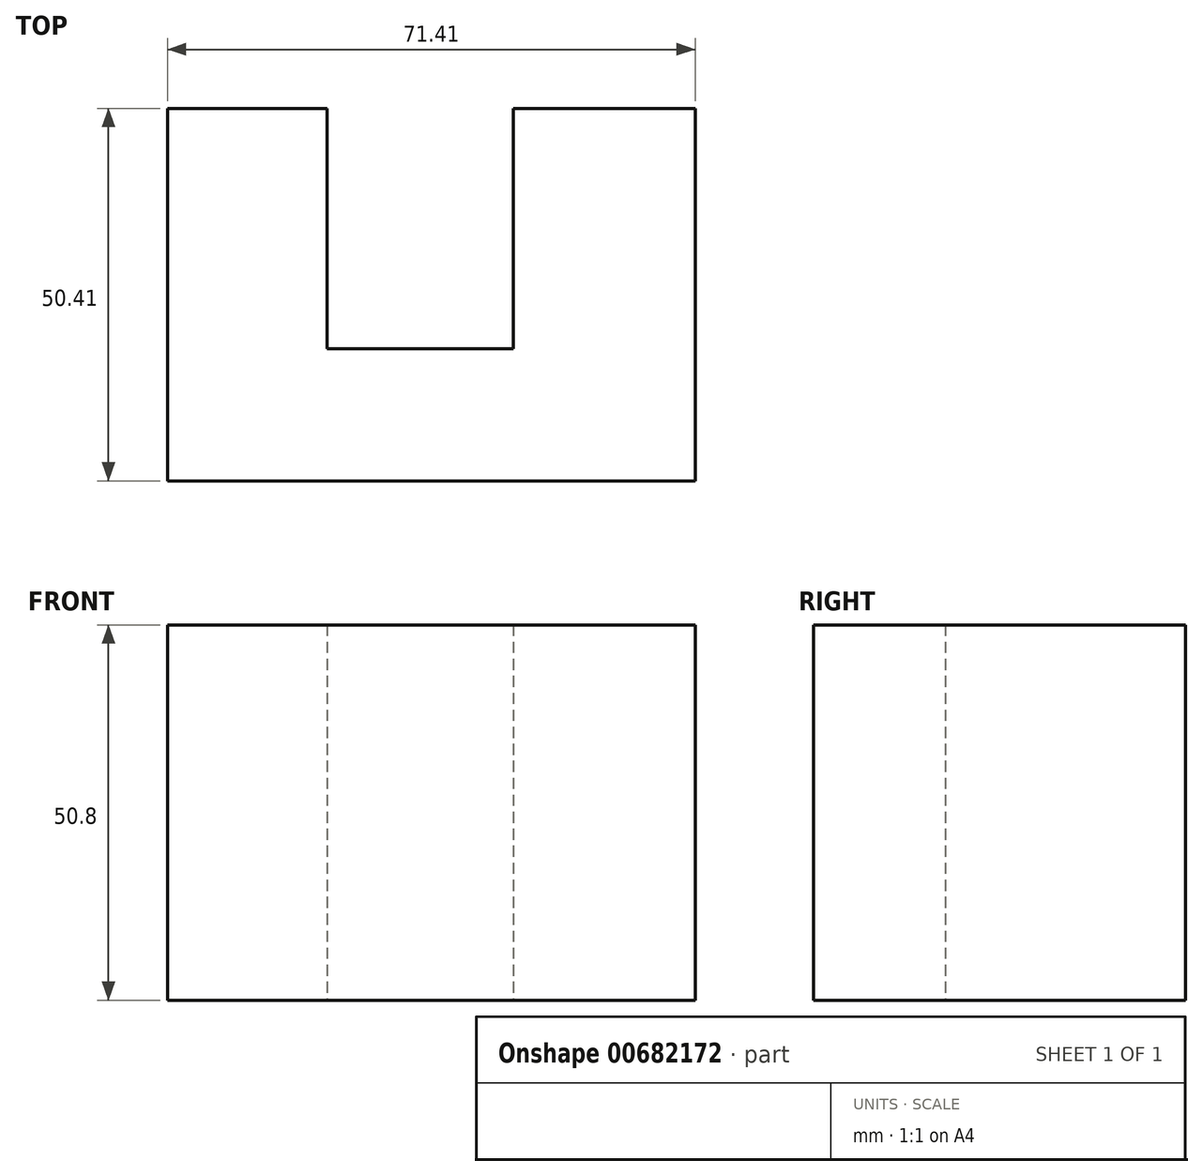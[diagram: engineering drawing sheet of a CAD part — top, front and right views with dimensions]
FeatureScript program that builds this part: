
annotation { "Feature Type Name" : "Feature", "Feature Type Description" : "" }
export const myFeature = defineFeature(function(context is Context, id is Id, definition is map)
    precondition{}
    {
        {
            var Q0;
            Q0=qCreatedBy(makeId("Top.planeOp"),FACE);
            var sketch = newSketch(context, id + "F0", { "sketchPlane" : qUnion([Q0])});
            skLineSegment(sketch, "E0", {"start": v(-43.82, 32.56) * mm, "end": v(-43.82, -17.85) * mm});
            skLineSegment(sketch, "E1", {"start": v(-43.82, -17.85) * mm, "end": v(27.6, -17.85) * mm});
            skLineSegment(sketch, "E2", {"start": v(27.6, -17.85) * mm, "end": v(27.6, 32.56) * mm});
            skLineSegment(sketch, "E3", {"start": v(27.6, 32.56) * mm, "end": v(2.96, 32.56) * mm});
            skLineSegment(sketch, "E4", {"start": v(2.96, 32.56) * mm, "end": v(2.96, 0) * mm});
            skLineSegment(sketch, "E5", {"start": v(2.96, 0) * mm, "end": v(-22.25, 0) * mm});
            skLineSegment(sketch, "E6", {"start": v(-22.25, 0) * mm, "end": v(-22.25, 32.56) * mm});
            skLineSegment(sketch, "E7", {"start": v(-22.25, 32.56) * mm, "end": v(-43.82, 32.56) * mm});
            skSolve(sketch);
        }
        {
            var Q0;
            Q0 = qSketchRegion(id + "F0", true);
            extrude(context, id + "F1", {"entities" : qUnion([Q0]), "depth" : 50.8 * mm, "offsetDistance" : 25.4 * mm});
        }
    });
